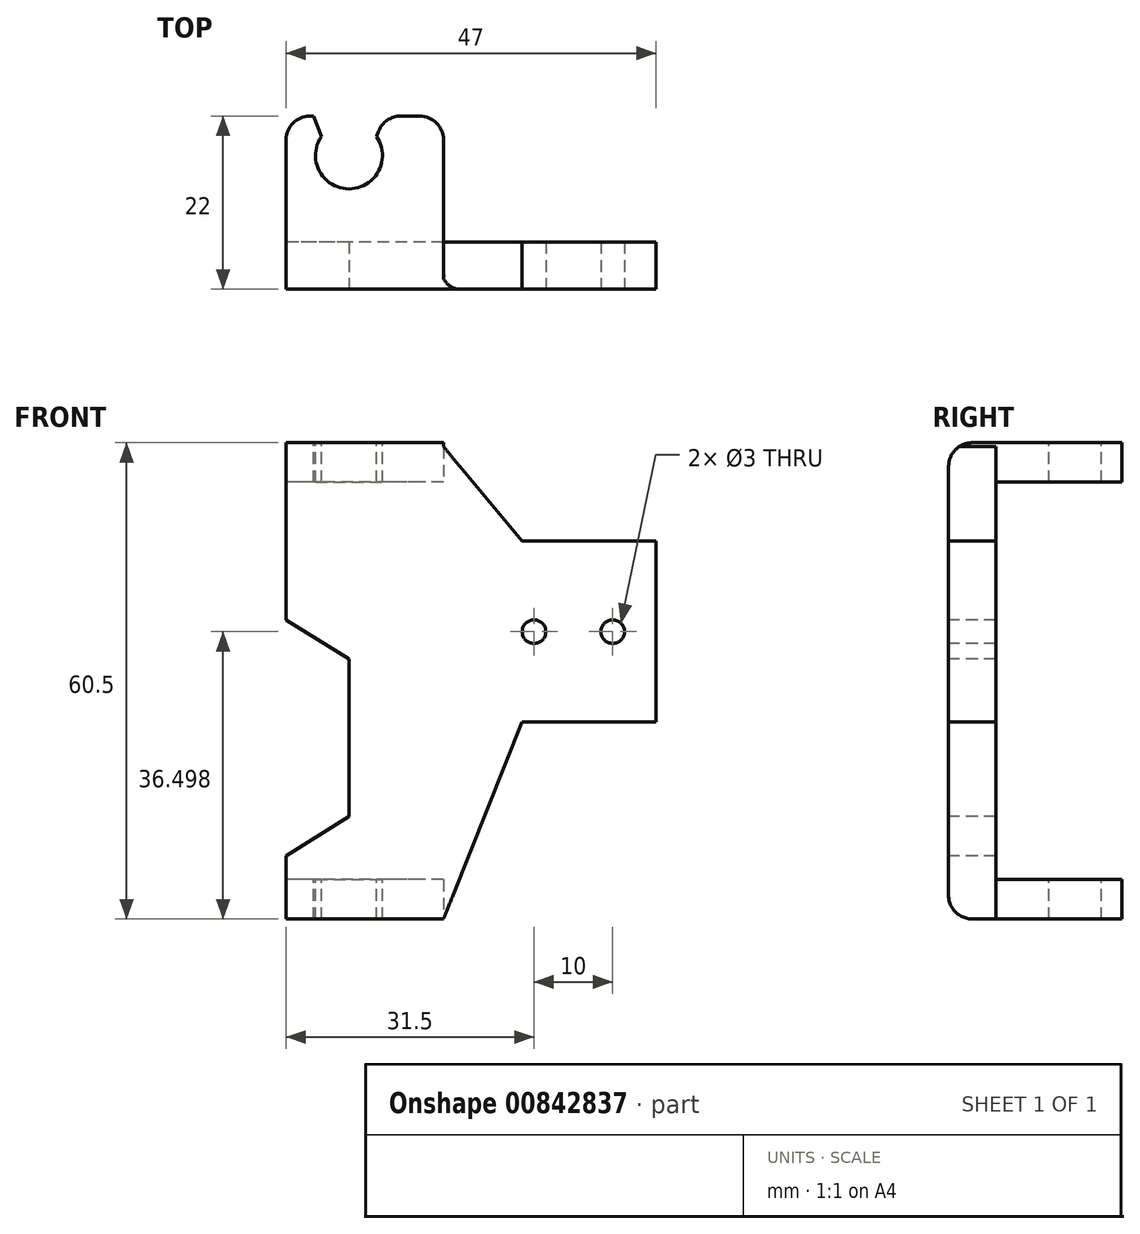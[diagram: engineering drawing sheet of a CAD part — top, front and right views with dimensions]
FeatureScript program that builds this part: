
annotation { "Feature Type Name" : "Feature", "Feature Type Description" : "" }
export const myFeature = defineFeature(function(context is Context, id is Id, definition is map)
    precondition{}
    {
        {
            var Q0;
            Q0=qCreatedBy(makeId("Right.planeOp"),FACE);
            var sketch = newSketch(context, id + "F0", { "sketchPlane" : qUnion([Q0])});
            skLineSegment(sketch, "E0.bottom", {"start": v(0, 23.68) * mm, "end": v(16, 23.68) * mm});
            skLineSegment(sketch, "E0.top", {"start": v(0, -26.82) * mm, "end": v(16, -26.82) * mm});
            skLineSegment(sketch, "E0.left", {"start": v(0, 23.68) * mm, "end": v(0, -26.82) * mm});
            skLineSegment(sketch, "E0.right", {"start": v(16, 23.68) * mm, "end": v(16, -26.82) * mm});
            skLineSegment(sketch, "E1.bottom", {"start": v(16, 28.68) * mm, "end": v(-6, 28.68) * mm});
            skLineSegment(sketch, "E1.top", {"start": v(16, -31.82) * mm, "end": v(-6, -31.82) * mm});
            skLineSegment(sketch, "E1.left", {"start": v(16, 28.68) * mm, "end": v(16, -31.82) * mm});
            skLineSegment(sketch, "E1.right", {"start": v(-6, 28.68) * mm, "end": v(-6, -31.82) * mm});
            skSolve(sketch);
        }
        {
            var Q0;
            {var subQ2=sQuery(id+"F0.wireOp",EDGE,"E0.bottom");Q0=makeQuery(id+"F0.imprint","IMPRINT",FACE,{"disambiguationData":[TD([[makeQuery(id+"F0.imprint","IMPRINT",EDGE,{"derivedFrom":subQ2}),1.0]])]});}
            extrude(context, id + "F1", {"entities" : qUnion([Q0]), "depth" : 20 * mm, "offsetDistance" : 25 * mm});
        }
        {
            var Q0;
            Q0=makeQuery(id+"F1.opExtrude","SWEPT_FACE",FACE,{"disambiguationData":[OSD([sQuery(id+"F0.wireOp",EDGE,"E1.bottom")])]});
            var sketch = newSketch(context, id + "F2", { "sketchPlane" : qUnion([Q0])});
            skCircle(sketch, "E2", {"center": v(8, 11) * mm, "radius": 4.25 * mm});
            skLineSegment(sketch, "E3", {"start": v(4.5, 13.41) * mm, "end": v(3.5, 16) * mm});
            skLineSegment(sketch, "E4", {"start": v(3.5, 16) * mm, "end": v(12.5, 16) * mm});
            skLineSegment(sketch, "E5", {"start": v(12.5, 16) * mm, "end": v(11.5, 13.41) * mm});
            skSolve(sketch);
        }
        {
            var Q0;
            Q0 = qSketchRegion(id + "F2", true);
            extrude(context, id + "F3", {"entities" : qUnion([Q0]), "operationType" : NewBodyOperationType.REMOVE, "oppositeDirection" : true, "depth" : 70 * mm, "offsetDistance" : 25 * mm});
        }
        {
            var Q0;
            Q0=makeQuery(id+"F1.opExtrude","SWEPT_FACE",FACE,{"disambiguationData":[OSD([sQuery(id+"F0.wireOp",EDGE,"E1.right")])]});
            var sketch = newSketch(context, id + "F4", { "sketchPlane" : qUnion([Q0])});
            skLineSegment(sketch, "E6.bottom", {"start": v(20, -6.82) * mm, "end": v(47, -6.82) * mm});
            skLineSegment(sketch, "E6.top", {"start": v(20, 16.18) * mm, "end": v(47, 16.18) * mm});
            skLineSegment(sketch, "E6.left", {"start": v(20, -6.82) * mm, "end": v(20, 16.18) * mm});
            skLineSegment(sketch, "E6.right", {"start": v(47, -6.82) * mm, "end": v(47, 16.18) * mm});
            skCircle(sketch, "E7", {"center": v(41.5, 4.68) * mm, "radius": 1.5 * mm});
            skCircle(sketch, "E8", {"center": v(31.5, 4.68) * mm, "radius": 1.5 * mm});
            skLineSegment(sketch, "E9", {"start": v(30, 16.18) * mm, "end": v(20, 16.18) * mm});
            skLineSegment(sketch, "E10", {"start": v(20, 28.18) * mm, "end": v(30, 16.18) * mm});
            skLineSegment(sketch, "E11", {"start": v(20, -6.82) * mm, "end": v(30, -6.82) * mm});
            skLineSegment(sketch, "E12", {"start": v(30, -6.82) * mm, "end": v(20, -31.82) * mm});
            skLineSegment(sketch, "E13", {"start": v(20, -31.82) * mm, "end": v(20, -6.82) * mm});
            skLineSegment(sketch, "E14", {"start": v(20, 16.18) * mm, "end": v(20, 28.18) * mm});
            skSolve(sketch);
        }
        {
            var Q0;
            Q0 = qSketchRegion(id + "F4", true);
            extrude(context, id + "F5", {"entities" : qUnion([Q0]), "operationType" : NewBodyOperationType.ADD, "oppositeDirection" : true, "depth" : 6 * mm, "offsetDistance" : 25 * mm});
        }
        {
            var Q0;
            {var subQ0=sQuery(id+"F0.wireOp",EDGE,"E1.left");Q0=makeQuery(id+"F1.opExtrude","CAP_EDGE",EDGE,{"disambiguationData":[OSD([subQ0]),TDD([makeQuery(id+"F0.imprint","IMPRINT",EDGE,{"disambiguationData":[TD([[makeQuery(id+"F0.imprint","INTERSECT",VERTEX,{"derivedFrom":[sQuery(id+"F0.wireOp",EDGE,"E1.bottom"),subQ0]}),-1.0]])],"derivedFrom":subQ0})])],"isStart":false});}
            var Q1;
            {var subQ0=sQuery(id+"F0.wireOp",EDGE,"E1.left");Q1=makeQuery(id+"F1.opExtrude","CAP_EDGE",EDGE,{"disambiguationData":[OSD([subQ0]),TDD([makeQuery(id+"F0.imprint","IMPRINT",EDGE,{"disambiguationData":[TD([[makeQuery(id+"F0.imprint","INTERSECT",VERTEX,{"derivedFrom":[sQuery(id+"F0.wireOp",EDGE,"E1.top"),subQ0]}),1.0]])],"derivedFrom":subQ0})])],"isStart":false});}
            var Q2;
            {var subQ0=sQuery(id+"F0.wireOp",EDGE,"E1.left");Q2=makeQuery(id+"F1.opExtrude","CAP_EDGE",EDGE,{"disambiguationData":[OSD([subQ0]),TDD([makeQuery(id+"F0.imprint","IMPRINT",EDGE,{"disambiguationData":[TD([[makeQuery(id+"F0.imprint","INTERSECT",VERTEX,{"derivedFrom":[sQuery(id+"F0.wireOp",EDGE,"E1.top"),subQ0]}),1.0]])],"derivedFrom":subQ0})])],"isStart":true});}
            var Q3;
            {var subQ0=sQuery(id+"F0.wireOp",EDGE,"E1.left");Q3=makeQuery(id+"F1.opExtrude","CAP_EDGE",EDGE,{"disambiguationData":[OSD([subQ0]),TDD([makeQuery(id+"F0.imprint","IMPRINT",EDGE,{"disambiguationData":[TD([[makeQuery(id+"F0.imprint","INTERSECT",VERTEX,{"derivedFrom":[sQuery(id+"F0.wireOp",EDGE,"E1.bottom"),subQ0]}),-1.0]])],"derivedFrom":subQ0})])],"isStart":true});}
            var Q4;
            {var subQ0=sQuery(id+"F0.wireOp",EDGE,"E1.left");var subQ1=sQuery(id+"F0.wireOp",EDGE,"E1.bottom");var subQ2=sQuery(id+"F2.wireOp",EDGE,"E5");Q4=makeQuery(id+"F3.boolean.opBoolean","COPY",EDGE,{"disambiguationData":[topologyDisambiguationEdgeConnected([makeQuery(id+"F1.opExtrude","SWEPT_FACE",FACE,{"disambiguationData":[OSD([subQ0]),TDD([makeQuery(id+"F0.imprint","IMPRINT",EDGE,{"disambiguationData":[TD([[makeQuery(id+"F0.imprint","INTERSECT",VERTEX,{"derivedFrom":[subQ1,subQ0]}),-1.0]])],"derivedFrom":subQ0})])]})])],"derivedFrom":makeQuery(id+"F3.opExtrude","SWEPT_EDGE",EDGE,{"disambiguationData":[OSD([subQ1,subQ0,sQuery(id+"F2.wireOp",EDGE,"E4"),subQ2])]})});}
            var Q5;
            {var subQ0=sQuery(id+"F0.wireOp",EDGE,"E1.left");var subQ1=sQuery(id+"F2.wireOp",EDGE,"E5");Q5=makeQuery(id+"F3.boolean.opBoolean","COPY",EDGE,{"disambiguationData":[topologyDisambiguationEdgeConnected([makeQuery(id+"F1.opExtrude","SWEPT_FACE",FACE,{"disambiguationData":[OSD([subQ0]),TDD([makeQuery(id+"F0.imprint","IMPRINT",EDGE,{"disambiguationData":[TD([[makeQuery(id+"F0.imprint","INTERSECT",VERTEX,{"derivedFrom":[sQuery(id+"F0.wireOp",EDGE,"E1.top"),subQ0]}),1.0]])],"derivedFrom":subQ0})])]})])],"derivedFrom":makeQuery(id+"F3.opExtrude","SWEPT_EDGE",EDGE,{"disambiguationData":[OSD([sQuery(id+"F0.wireOp",EDGE,"E1.bottom"),subQ0,sQuery(id+"F2.wireOp",EDGE,"E4"),subQ1])]})});}
            var Q6;
            {var subQ0=sQuery(id+"F0.wireOp",EDGE,"E1.left");var subQ1=sQuery(id+"F0.wireOp",EDGE,"E1.bottom");var subQ2=sQuery(id+"F2.wireOp",EDGE,"E3");Q6=makeQuery(id+"F3.boolean.opBoolean","COPY",EDGE,{"disambiguationData":[topologyDisambiguationEdgeConnected([makeQuery(id+"F1.opExtrude","SWEPT_FACE",FACE,{"disambiguationData":[OSD([subQ0]),TDD([makeQuery(id+"F0.imprint","IMPRINT",EDGE,{"disambiguationData":[TD([[makeQuery(id+"F0.imprint","INTERSECT",VERTEX,{"derivedFrom":[subQ1,subQ0]}),-1.0]])],"derivedFrom":subQ0})])]})])],"derivedFrom":makeQuery(id+"F3.opExtrude","SWEPT_EDGE",EDGE,{"disambiguationData":[OSD([subQ1,subQ0,subQ2,sQuery(id+"F2.wireOp",EDGE,"E4")])]})});}
            var Q7;
            {var subQ0=sQuery(id+"F0.wireOp",EDGE,"E1.left");var subQ1=sQuery(id+"F2.wireOp",EDGE,"E3");Q7=makeQuery(id+"F3.boolean.opBoolean","COPY",EDGE,{"disambiguationData":[topologyDisambiguationEdgeConnected([makeQuery(id+"F1.opExtrude","SWEPT_FACE",FACE,{"disambiguationData":[OSD([subQ0]),TDD([makeQuery(id+"F0.imprint","IMPRINT",EDGE,{"disambiguationData":[TD([[makeQuery(id+"F0.imprint","INTERSECT",VERTEX,{"derivedFrom":[sQuery(id+"F0.wireOp",EDGE,"E1.top"),subQ0]}),1.0]])],"derivedFrom":subQ0})])]})])],"derivedFrom":makeQuery(id+"F3.opExtrude","SWEPT_EDGE",EDGE,{"disambiguationData":[OSD([sQuery(id+"F0.wireOp",EDGE,"E1.bottom"),subQ0,subQ1,sQuery(id+"F2.wireOp",EDGE,"E4")])]})});}
            var Q8;
            Q8=makeQuery(id+"F1.opExtrude","SWEPT_EDGE",EDGE,{"disambiguationData":[OSD([sQuery(id+"F0.wireOp",EDGE,"E1.bottom"),sQuery(id+"F0.wireOp",EDGE,"E1.right")])]});
            var Q9;
            Q9=makeQuery(id+"F1.opExtrude","SWEPT_EDGE",EDGE,{"disambiguationData":[OSD([sQuery(id+"F0.wireOp",EDGE,"E1.top"),sQuery(id+"F0.wireOp",EDGE,"E1.right")])]});
            fillet(context, id + "F6", {"entities" : qUnion([Q0, Q1, Q2, Q3, Q4, Q5, Q6, Q7, Q8, Q9]), "radius" : 3 * mm, "tangentPropagation" : true, "allowEdgeOverflow" : false});
        }
        {
            var Q0;
            Q0=makeQuery(id+"F5.boolean.opBoolean","MERGE",FACE,{"derivedFrom":[makeQuery(id+"F1.opExtrude","SWEPT_FACE",FACE,{"disambiguationData":[OSD([sQuery(id+"F0.wireOp",EDGE,"E1.right")])]}),makeQuery(id+"F5.opExtrude","CAP_FACE",FACE,{"disambiguationData":[OSD([sQuery(id+"F4.wireOp",EDGE,"E6.bottom"),sQuery(id+"F4.wireOp",EDGE,"E6.top"),sQuery(id+"F4.wireOp",EDGE,"E6.left"),sQuery(id+"F4.wireOp",EDGE,"E6.right"),sQuery(id+"F4.wireOp",EDGE,"E7"),sQuery(id+"F4.wireOp",EDGE,"E8"),sQuery(id+"F4.wireOp",EDGE,"E10"),sQuery(id+"F4.wireOp",EDGE,"E12"),sQuery(id+"F4.wireOp",EDGE,"E13"),sQuery(id+"F4.wireOp",EDGE,"E14")])],"isStart":true})]});
            var sketch = newSketch(context, id + "F7", { "sketchPlane" : qUnion([Q0])});
            skLineSegment(sketch, "E15", {"start": v(0, -23.82) * mm, "end": v(8, -18.82) * mm});
            skLineSegment(sketch, "E16", {"start": v(8, -18.82) * mm, "end": v(8, 1.18) * mm});
            skLineSegment(sketch, "E17", {"start": v(8, 1.18) * mm, "end": v(0, 6.18) * mm});
            skLineSegment(sketch, "E18", {"start": v(0, 6.18) * mm, "end": v(0, -23.82) * mm});
            skSolve(sketch);
        }
        {
            var Q0;
            Q0 = qSketchRegion(id + "F7", true);
            extrude(context, id + "F8", {"entities" : qUnion([Q0]), "operationType" : NewBodyOperationType.REMOVE, "oppositeDirection" : true, "depth" : 25 * mm, "offsetDistance" : 25 * mm});
        }
        {
            var Q0;
            Q0 = qSketchRegion(id + "F7", true);
            extrude(context, id + "F9", {"entities" : qUnion([Q0]), "operationType" : NewBodyOperationType.REMOVE, "oppositeDirection" : true, "depth" : 25 * mm, "offsetDistance" : 25 * mm});
        }
    });
